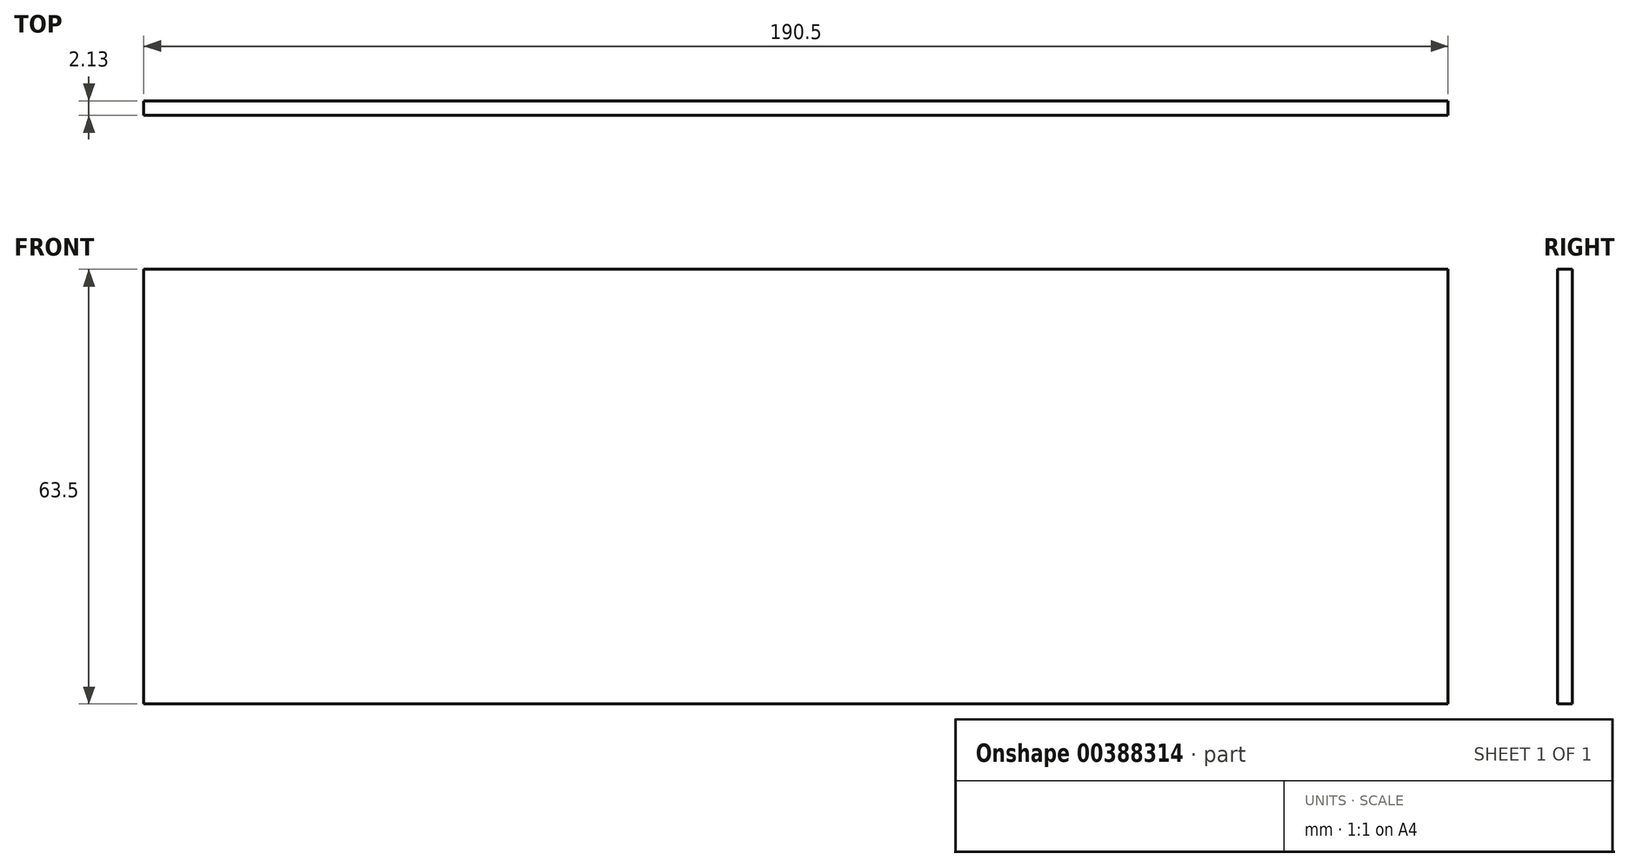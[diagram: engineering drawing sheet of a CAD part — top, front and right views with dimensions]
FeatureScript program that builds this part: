
annotation { "Feature Type Name" : "Feature", "Feature Type Description" : "" }
export const myFeature = defineFeature(function(context is Context, id is Id, definition is map)
    precondition{}
    {
        {
            var Q0;
            Q0=qCreatedBy(makeId("Front.planeOp"),FACE);
            var sketch = newSketch(context, id + "F0", { "sketchPlane" : qUnion([Q0])});
            skLineSegment(sketch, "E0", {"start": v(-87.12, -3.92) * mm, "end": v(103.38, -3.92) * mm});
            skLineSegment(sketch, "E1", {"start": v(103.38, -3.92) * mm, "end": v(103.38, -67.42) * mm});
            skLineSegment(sketch, "E2", {"start": v(103.38, -67.42) * mm, "end": v(-87.12, -67.42) * mm});
            skLineSegment(sketch, "E3", {"start": v(-87.12, -67.42) * mm, "end": v(-87.12, -3.92) * mm});
            skSolve(sketch);
        }
        {
            var Q0;
            Q0=qSketchRegion(id+"F0",true);
            extrude(context, id + "F1", {"entities" : qUnion([Q0]), "depth" : 2.13 * mm});
        }
    });
